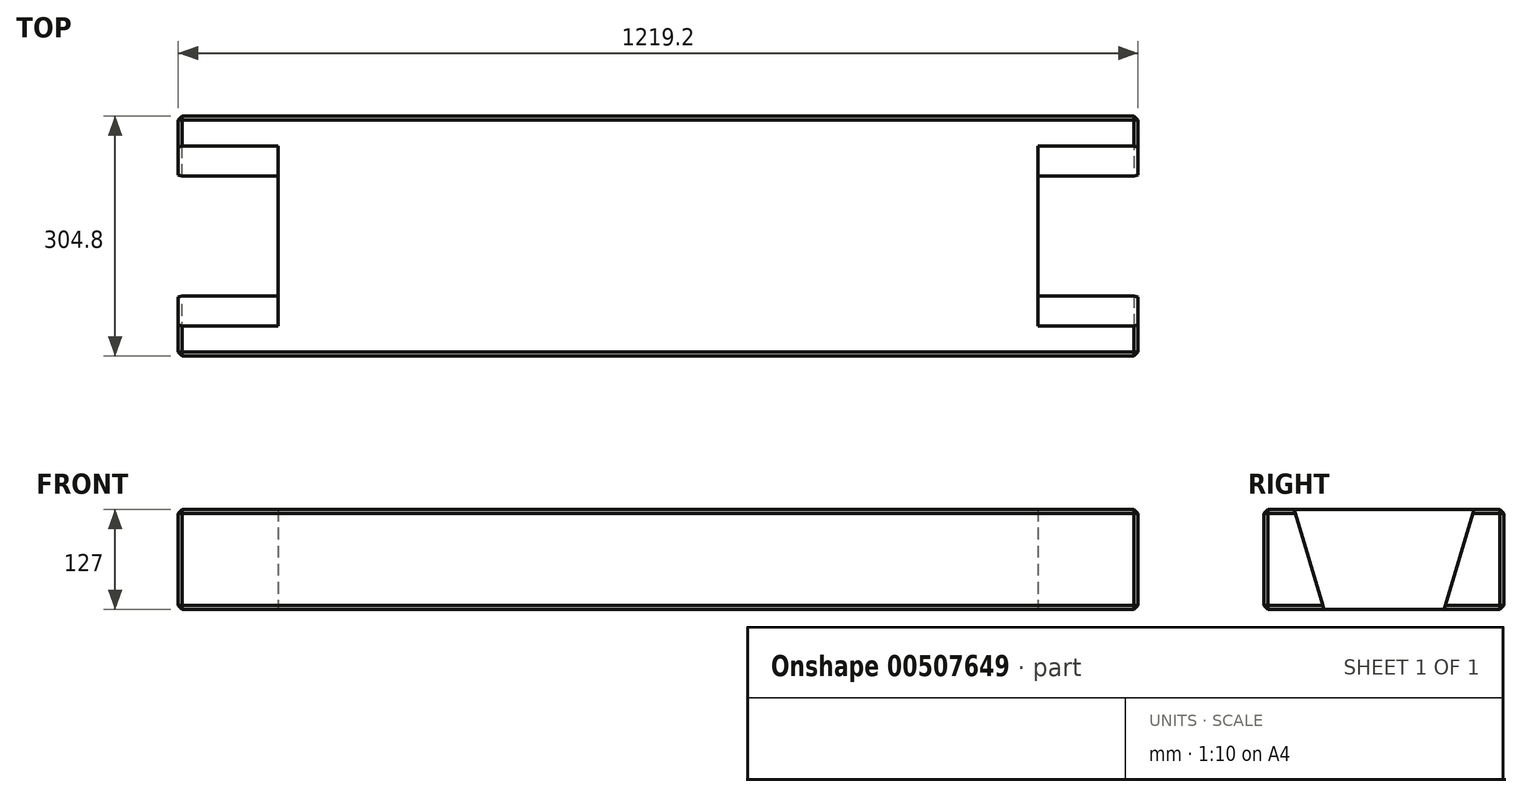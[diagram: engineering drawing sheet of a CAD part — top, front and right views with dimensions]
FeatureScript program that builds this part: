
annotation { "Feature Type Name" : "Feature", "Feature Type Description" : "" }
export const myFeature = defineFeature(function(context is Context, id is Id, definition is map)
    precondition{}
    {
        {
            var Q0;
            Q0=qCreatedBy(makeId("Top.planeOp"),FACE);
            var sketch = newSketch(context, id + "F0", { "sketchPlane" : qUnion([Q0])});
            skLineSegment(sketch, "E0.bottom", {"start": v(-609.6, 152.4) * mm, "end": v(609.6, 152.4) * mm});
            skLineSegment(sketch, "E0.top", {"start": v(-609.6, -152.4) * mm, "end": v(609.6, -152.4) * mm});
            skLineSegment(sketch, "E0.left", {"start": v(-609.6, 152.4) * mm, "end": v(-609.6, -152.4) * mm});
            skLineSegment(sketch, "E0.right", {"start": v(609.6, 152.4) * mm, "end": v(609.6, -152.4) * mm});
            skSolve(sketch);
        }
        {
            var Q0;
            Q0 = qSketchRegion(id + "F0", true);
            extrude(context, id + "F1", {"entities" : qUnion([Q0]), "depth" : 63.5 * mm, "hasSecondDirection" : true, "secondDirectionOppositeDirection" : true, "secondDirectionDepth" : 63.5 * mm});
        }
        {
            var Q0;
            Q0=makeQuery(id+"F1.opExtrude","SWEPT_FACE",FACE,{"disambiguationData":[OSD([sQuery(id+"F0.wireOp",EDGE,"E0.right")])]});
            var sketch = newSketch(context, id + "F2", { "sketchPlane" : qUnion([Q0])});
            skLineSegment(sketch, "E1", {"start": v(0, 63.5) * mm, "end": v(-114.3, 63.5) * mm});
            skLineSegment(sketch, "E2", {"start": v(-114.3, 63.5) * mm, "end": v(-76.2, -63.5) * mm});
            skLineSegment(sketch, "E3", {"start": v(-76.2, -63.5) * mm, "end": v(0, -63.5) * mm});
            skLineSegment(sketch, "E4.MirrorCS", {"start": v(0, 63.5) * mm, "end": v(114.3, 63.5) * mm});
            skLineSegment(sketch, "E5.MirrorCS", {"start": v(114.3, 63.5) * mm, "end": v(76.2, -63.5) * mm});
            skLineSegment(sketch, "E6.MirrorCS", {"start": v(76.2, -63.5) * mm, "end": v(0, -63.5) * mm});
            skSolve(sketch);
        }
        {
            var Q0;
            Q0 = qSketchRegion(id + "F2", true);
            extrude(context, id + "F3", {"entities" : qUnion([Q0]), "operationType" : NewBodyOperationType.REMOVE, "oppositeDirection" : true, "depth" : 127 * mm});
        }
        {
            var Q0;
            Q0=makeQuery(id+"F1.opExtrude","SWEPT_FACE",FACE,{"disambiguationData":[OSD([sQuery(id+"F0.wireOp",EDGE,"E0.left")])]});
            var sketch = newSketch(context, id + "F4", { "sketchPlane" : qUnion([Q0])});
            skLineSegment(sketch, "E7", {"start": v(0, 63.5) * mm, "end": v(-114.3, 63.5) * mm});
            skLineSegment(sketch, "E8", {"start": v(-114.3, 63.5) * mm, "end": v(-76.2, -63.5) * mm});
            skLineSegment(sketch, "E9", {"start": v(-76.2, -63.5) * mm, "end": v(0, -63.5) * mm});
            skLineSegment(sketch, "E10.MirrorCS", {"start": v(0, 63.5) * mm, "end": v(114.3, 63.5) * mm});
            skLineSegment(sketch, "E11.MirrorCS", {"start": v(114.3, 63.5) * mm, "end": v(76.2, -63.5) * mm});
            skLineSegment(sketch, "E12.MirrorCS", {"start": v(76.2, -63.5) * mm, "end": v(0, -63.5) * mm});
            skSolve(sketch);
        }
        {
            var Q0;
            Q0 = qSketchRegion(id + "F4", true);
            extrude(context, id + "F5", {"entities" : qUnion([Q0]), "operationType" : NewBodyOperationType.REMOVE, "oppositeDirection" : true, "depth" : 127 * mm});
        }
        {
            var Q0;
            {var subQ0=sQuery(id+"F0.wireOp",EDGE,"E0.bottom");var subQ1=sQuery(id+"F0.wireOp",EDGE,"E0.right");Q0=makeQuery(id+"F3.boolean.opBoolean","SPLIT",EDGE,{"disambiguationData":[TD([makeQuery(id+"F1.opExtrude","SWEPT_FACE",FACE,{"disambiguationData":[OSD([subQ0])]})])],"derivedFrom":makeQuery(id+"F1.opExtrude","CAP_EDGE",EDGE,{"disambiguationData":[OSD([subQ1])],"isStart":false})});}
            var Q1;
            Q1=makeQuery(id+"F1.opExtrude","CAP_EDGE",EDGE,{"disambiguationData":[OSD([sQuery(id+"F0.wireOp",EDGE,"E0.bottom")])],"isStart":false});
            var Q2;
            {var subQ0=sQuery(id+"F0.wireOp",EDGE,"E0.bottom");var subQ1=sQuery(id+"F0.wireOp",EDGE,"E0.left");Q2=makeQuery(id+"F5.boolean.opBoolean","SPLIT",EDGE,{"disambiguationData":[TD([makeQuery(id+"F1.opExtrude","SWEPT_FACE",FACE,{"disambiguationData":[OSD([subQ0])]})])],"derivedFrom":makeQuery(id+"F1.opExtrude","CAP_EDGE",EDGE,{"disambiguationData":[OSD([subQ1])],"isStart":false})});}
            var Q3;
            Q3=makeQuery(id+"F5.boolean.opBoolean","COPY",EDGE,{"derivedFrom":makeQuery(id+"F5.opExtrude","SWEPT_EDGE",EDGE,{"disambiguationData":[OSD([sQuery(id+"F0.wireOp",EDGE,"E0.left"),sQuery(id+"F4.wireOp",EDGE,"E7"),sQuery(id+"F4.wireOp",EDGE,"E8")])]})});
            var Q4;
            Q4=makeQuery(id+"F5.boolean.opBoolean","COPY",EDGE,{"derivedFrom":makeQuery(id+"F5.opExtrude","CAP_EDGE",EDGE,{"disambiguationData":[OSD([sQuery(id+"F4.wireOp",EDGE,"E7"),sQuery(id+"F4.wireOp",EDGE,"E10.MirrorCS")])],"isStart":false})});
            var Q5;
            Q5=makeQuery(id+"F5.boolean.opBoolean","COPY",EDGE,{"derivedFrom":makeQuery(id+"F5.opExtrude","SWEPT_EDGE",EDGE,{"disambiguationData":[OSD([sQuery(id+"F0.wireOp",EDGE,"E0.left"),sQuery(id+"F4.wireOp",EDGE,"E10.MirrorCS"),sQuery(id+"F4.wireOp",EDGE,"E11.MirrorCS")])]})});
            var Q6;
            {var subQ0=sQuery(id+"F0.wireOp",EDGE,"E0.left");var subQ1=sQuery(id+"F0.wireOp",EDGE,"E0.top");Q6=makeQuery(id+"F5.boolean.opBoolean","SPLIT",EDGE,{"disambiguationData":[TD([makeQuery(id+"F1.opExtrude","SWEPT_FACE",FACE,{"disambiguationData":[OSD([subQ1])]})])],"derivedFrom":makeQuery(id+"F1.opExtrude","CAP_EDGE",EDGE,{"disambiguationData":[OSD([subQ0])],"isStart":false})});}
            var Q7;
            Q7=makeQuery(id+"F1.opExtrude","CAP_EDGE",EDGE,{"disambiguationData":[OSD([sQuery(id+"F0.wireOp",EDGE,"E0.top")])],"isStart":false});
            var Q8;
            {var subQ0=sQuery(id+"F0.wireOp",EDGE,"E0.right");var subQ1=sQuery(id+"F0.wireOp",EDGE,"E0.top");Q8=makeQuery(id+"F3.boolean.opBoolean","SPLIT",EDGE,{"disambiguationData":[TD([makeQuery(id+"F1.opExtrude","SWEPT_FACE",FACE,{"disambiguationData":[OSD([subQ1])]})])],"derivedFrom":makeQuery(id+"F1.opExtrude","CAP_EDGE",EDGE,{"disambiguationData":[OSD([subQ0])],"isStart":false})});}
            var Q9;
            Q9=makeQuery(id+"F3.boolean.opBoolean","COPY",EDGE,{"derivedFrom":makeQuery(id+"F3.opExtrude","SWEPT_EDGE",EDGE,{"disambiguationData":[OSD([sQuery(id+"F0.wireOp",EDGE,"E0.right"),sQuery(id+"F2.wireOp",EDGE,"E1"),sQuery(id+"F2.wireOp",EDGE,"E2")])]})});
            var Q10;
            Q10=makeQuery(id+"F3.boolean.opBoolean","COPY",EDGE,{"derivedFrom":makeQuery(id+"F3.opExtrude","CAP_EDGE",EDGE,{"disambiguationData":[OSD([sQuery(id+"F2.wireOp",EDGE,"E1"),sQuery(id+"F2.wireOp",EDGE,"E4.MirrorCS")])],"isStart":false})});
            var Q11;
            Q11=makeQuery(id+"F3.boolean.opBoolean","COPY",EDGE,{"derivedFrom":makeQuery(id+"F3.opExtrude","SWEPT_EDGE",EDGE,{"disambiguationData":[OSD([sQuery(id+"F0.wireOp",EDGE,"E0.right"),sQuery(id+"F2.wireOp",EDGE,"E4.MirrorCS"),sQuery(id+"F2.wireOp",EDGE,"E5.MirrorCS")])]})});
            var Q12;
            Q12=makeQuery(id+"F1.opExtrude","SWEPT_EDGE",EDGE,{"disambiguationData":[OSD([sQuery(id+"F0.wireOp",EDGE,"E0.bottom"),sQuery(id+"F0.wireOp",EDGE,"E0.right")])]});
            var Q13;
            Q13=makeQuery(id+"F3.boolean.opBoolean","COPY",EDGE,{"derivedFrom":makeQuery(id+"F3.opExtrude","CAP_EDGE",EDGE,{"disambiguationData":[OSD([sQuery(id+"F2.wireOp",EDGE,"E5.MirrorCS")])],"isStart":true})});
            var Q14;
            Q14=makeQuery(id+"F3.boolean.opBoolean","COPY",EDGE,{"derivedFrom":makeQuery(id+"F3.opExtrude","CAP_EDGE",EDGE,{"disambiguationData":[OSD([sQuery(id+"F2.wireOp",EDGE,"E2")])],"isStart":true})});
            var Q15;
            Q15=makeQuery(id+"F1.opExtrude","SWEPT_EDGE",EDGE,{"disambiguationData":[OSD([sQuery(id+"F0.wireOp",EDGE,"E0.top"),sQuery(id+"F0.wireOp",EDGE,"E0.right")])]});
            var Q16;
            Q16=makeQuery(id+"F1.opExtrude","SWEPT_EDGE",EDGE,{"disambiguationData":[OSD([sQuery(id+"F0.wireOp",EDGE,"E0.top"),sQuery(id+"F0.wireOp",EDGE,"E0.left")])]});
            var Q17;
            Q17=makeQuery(id+"F5.boolean.opBoolean","COPY",EDGE,{"derivedFrom":makeQuery(id+"F5.opExtrude","CAP_EDGE",EDGE,{"disambiguationData":[OSD([sQuery(id+"F4.wireOp",EDGE,"E11.MirrorCS")])],"isStart":true})});
            var Q18;
            Q18=makeQuery(id+"F5.boolean.opBoolean","COPY",EDGE,{"derivedFrom":makeQuery(id+"F5.opExtrude","CAP_EDGE",EDGE,{"disambiguationData":[OSD([sQuery(id+"F4.wireOp",EDGE,"E8")])],"isStart":true})});
            var Q19;
            Q19=makeQuery(id+"F1.opExtrude","SWEPT_EDGE",EDGE,{"disambiguationData":[OSD([sQuery(id+"F0.wireOp",EDGE,"E0.bottom"),sQuery(id+"F0.wireOp",EDGE,"E0.left")])]});
            var Q20;
            {var subQ0=sQuery(id+"F0.wireOp",EDGE,"E0.bottom");var subQ1=sQuery(id+"F0.wireOp",EDGE,"E0.left");Q20=makeQuery(id+"F5.boolean.opBoolean","SPLIT",EDGE,{"disambiguationData":[TD([makeQuery(id+"F1.opExtrude","SWEPT_FACE",FACE,{"disambiguationData":[OSD([subQ0])]})])],"derivedFrom":makeQuery(id+"F1.opExtrude","CAP_EDGE",EDGE,{"disambiguationData":[OSD([subQ1])],"isStart":true})});}
            var Q21;
            Q21=makeQuery(id+"F1.opExtrude","CAP_EDGE",EDGE,{"disambiguationData":[OSD([sQuery(id+"F0.wireOp",EDGE,"E0.bottom")])],"isStart":true});
            var Q22;
            {var subQ0=sQuery(id+"F0.wireOp",EDGE,"E0.bottom");var subQ1=sQuery(id+"F0.wireOp",EDGE,"E0.right");Q22=makeQuery(id+"F3.boolean.opBoolean","SPLIT",EDGE,{"disambiguationData":[TD([makeQuery(id+"F1.opExtrude","SWEPT_FACE",FACE,{"disambiguationData":[OSD([subQ0])]})])],"derivedFrom":makeQuery(id+"F1.opExtrude","CAP_EDGE",EDGE,{"disambiguationData":[OSD([subQ1])],"isStart":true})});}
            var Q23;
            Q23=makeQuery(id+"F3.boolean.opBoolean","COPY",EDGE,{"derivedFrom":makeQuery(id+"F3.opExtrude","SWEPT_EDGE",EDGE,{"disambiguationData":[OSD([sQuery(id+"F0.wireOp",EDGE,"E0.right"),sQuery(id+"F2.wireOp",EDGE,"E5.MirrorCS"),sQuery(id+"F2.wireOp",EDGE,"E6.MirrorCS")])]})});
            var Q24;
            Q24=makeQuery(id+"F3.boolean.opBoolean","COPY",EDGE,{"derivedFrom":makeQuery(id+"F3.opExtrude","CAP_EDGE",EDGE,{"disambiguationData":[OSD([sQuery(id+"F2.wireOp",EDGE,"E3"),sQuery(id+"F2.wireOp",EDGE,"E6.MirrorCS")])],"isStart":false})});
            var Q25;
            Q25=makeQuery(id+"F3.boolean.opBoolean","COPY",EDGE,{"derivedFrom":makeQuery(id+"F3.opExtrude","SWEPT_EDGE",EDGE,{"disambiguationData":[OSD([sQuery(id+"F0.wireOp",EDGE,"E0.right"),sQuery(id+"F2.wireOp",EDGE,"E2"),sQuery(id+"F2.wireOp",EDGE,"E3")])]})});
            var Q26;
            {var subQ0=sQuery(id+"F0.wireOp",EDGE,"E0.right");var subQ1=sQuery(id+"F0.wireOp",EDGE,"E0.top");Q26=makeQuery(id+"F3.boolean.opBoolean","SPLIT",EDGE,{"disambiguationData":[TD([makeQuery(id+"F1.opExtrude","SWEPT_FACE",FACE,{"disambiguationData":[OSD([subQ1])]})])],"derivedFrom":makeQuery(id+"F1.opExtrude","CAP_EDGE",EDGE,{"disambiguationData":[OSD([subQ0])],"isStart":true})});}
            var Q27;
            Q27=makeQuery(id+"F1.opExtrude","CAP_EDGE",EDGE,{"disambiguationData":[OSD([sQuery(id+"F0.wireOp",EDGE,"E0.top")])],"isStart":true});
            var Q28;
            {var subQ0=sQuery(id+"F0.wireOp",EDGE,"E0.left");var subQ1=sQuery(id+"F0.wireOp",EDGE,"E0.top");Q28=makeQuery(id+"F5.boolean.opBoolean","SPLIT",EDGE,{"disambiguationData":[TD([makeQuery(id+"F1.opExtrude","SWEPT_FACE",FACE,{"disambiguationData":[OSD([subQ1])]})])],"derivedFrom":makeQuery(id+"F1.opExtrude","CAP_EDGE",EDGE,{"disambiguationData":[OSD([subQ0])],"isStart":true})});}
            var Q29;
            Q29=makeQuery(id+"F5.boolean.opBoolean","COPY",EDGE,{"derivedFrom":makeQuery(id+"F5.opExtrude","SWEPT_EDGE",EDGE,{"disambiguationData":[OSD([sQuery(id+"F0.wireOp",EDGE,"E0.left"),sQuery(id+"F4.wireOp",EDGE,"E11.MirrorCS"),sQuery(id+"F4.wireOp",EDGE,"E12.MirrorCS")])]})});
            var Q30;
            Q30=makeQuery(id+"F5.boolean.opBoolean","COPY",EDGE,{"derivedFrom":makeQuery(id+"F5.opExtrude","CAP_EDGE",EDGE,{"disambiguationData":[OSD([sQuery(id+"F4.wireOp",EDGE,"E9"),sQuery(id+"F4.wireOp",EDGE,"E12.MirrorCS")])],"isStart":false})});
            var Q31;
            Q31=makeQuery(id+"F5.boolean.opBoolean","COPY",EDGE,{"derivedFrom":makeQuery(id+"F5.opExtrude","SWEPT_EDGE",EDGE,{"disambiguationData":[OSD([sQuery(id+"F0.wireOp",EDGE,"E0.left"),sQuery(id+"F4.wireOp",EDGE,"E8"),sQuery(id+"F4.wireOp",EDGE,"E9")])]})});
            chamfer(context, id + "F6", {"entities" : qUnion([Q0, Q1, Q2, Q3, Q4, Q5, Q6, Q7, Q8, Q9, Q10, Q11, Q12, Q13, Q14, Q15, Q16, Q17, Q18, Q19, Q20, Q21, Q22, Q23, Q24, Q25, Q26, Q27, Q28, Q29, Q30, Q31]), "width" : 5.08 * mm, "tangentPropagation" : true});
        }
    });
